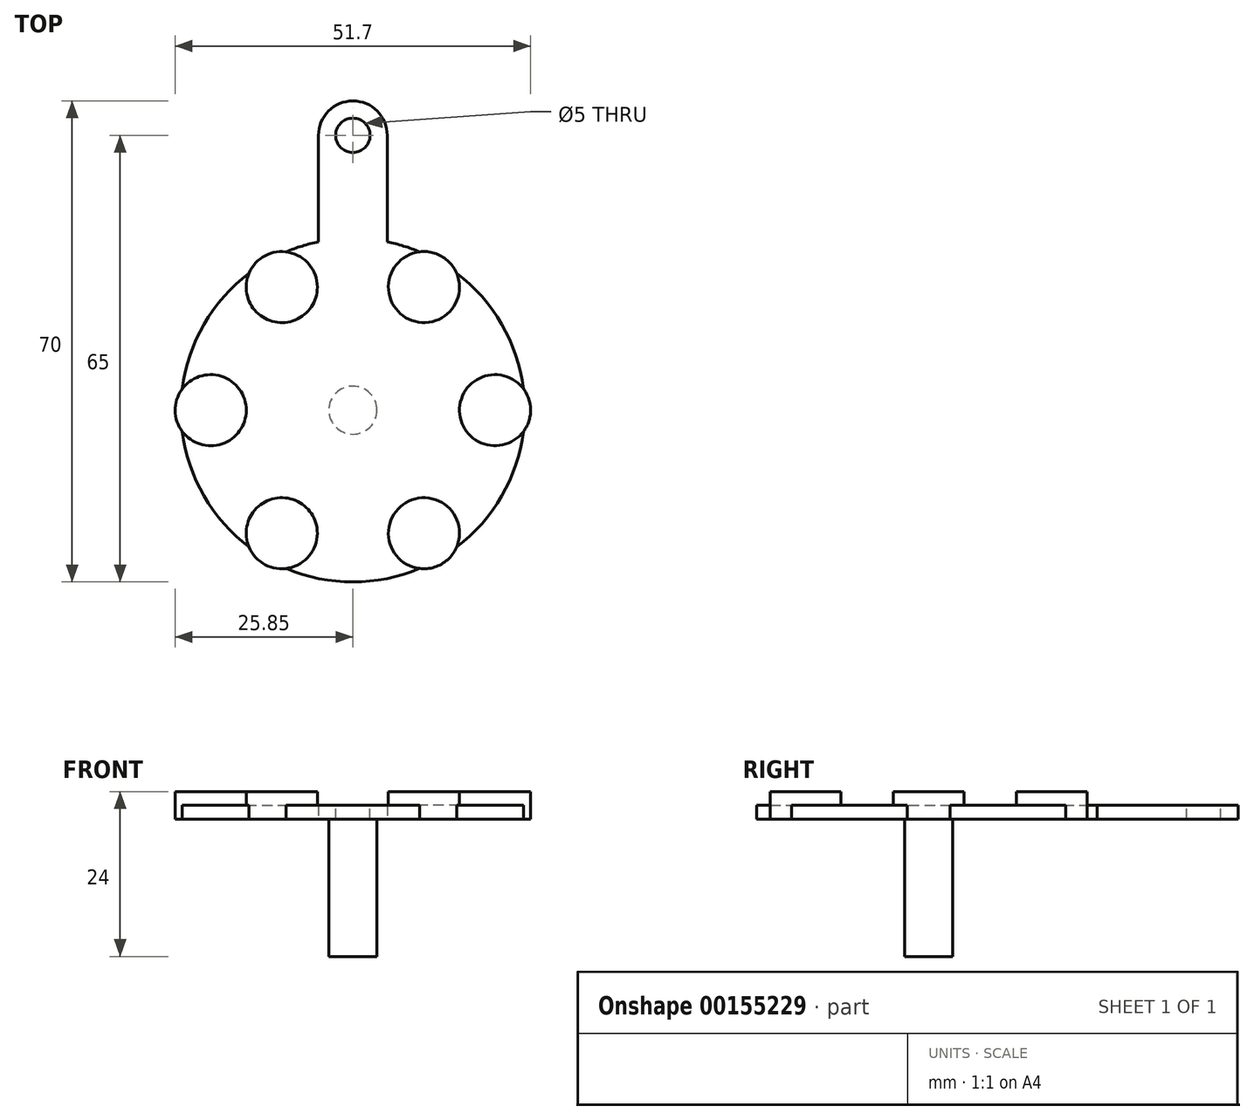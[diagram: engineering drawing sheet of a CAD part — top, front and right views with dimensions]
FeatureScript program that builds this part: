
annotation { "Feature Type Name" : "Feature", "Feature Type Description" : "" }
export const myFeature = defineFeature(function(context is Context, id is Id, definition is map)
    precondition{}
    {
        {
            var Q0;
            Q0=qCreatedBy(makeId("Top.planeOp"),FACE);
            var sketch = newSketch(context, id + "F0", { "sketchPlane" : qUnion([Q0])});
            skCircle(sketch, "E0", {"center": v(0, 0) * mm, "radius": 3.5 * mm});
            skSolve(sketch);
        }
        {
            var Q0;
            Q0 = qSketchRegion(id + "F0", true);
            extrude(context, id + "F1", {"entities" : qUnion([Q0]), "oppositeDirection" : true, "depth" : 20 * mm});
        }
        {
            var Q0;
            Q0=qCreatedBy(makeId("Top.planeOp"),FACE);
            var sketch = newSketch(context, id + "F2", { "sketchPlane" : qUnion([Q0])});
            skCircle(sketch, "E1", {"center": v(0, 0) * mm, "radius": 25 * mm});
            skSolve(sketch);
        }
        {
            var Q0;
            Q0 = qSketchRegion(id + "F2", true);
            extrude(context, id + "F3", {"entities" : qUnion([Q0]), "operationType" : NewBodyOperationType.ADD, "depth" : 2 * mm});
        }
        {
            var Q0;
            Q0=qCreatedBy(makeId("Top.planeOp"),FACE);
            var sketch = newSketch(context, id + "F4", { "sketchPlane" : qUnion([Q0])});
            skCircle(sketch, "E2", {"center": v(-20.68, 0) * mm, "radius": 5.17 * mm});
            skCircle(sketch, "E3.1.0", {"center": v(-10.34, -17.9) * mm, "radius": 5.17 * mm});
            skCircle(sketch, "E3.2.0", {"center": v(10.34, -17.9) * mm, "radius": 5.17 * mm});
            skCircle(sketch, "E3.3.0", {"center": v(20.68, 0) * mm, "radius": 5.17 * mm});
            skCircle(sketch, "E3.4.0", {"center": v(10.34, 17.9) * mm, "radius": 5.17 * mm});
            skCircle(sketch, "E3.5.0", {"center": v(-10.34, 17.9) * mm, "radius": 5.17 * mm});
            skPoint(sketch, "E3.center", {"position": v(0, 0) * mm});
            skSolve(sketch);
        }
        {
            var Q0;
            Q0 = qSketchRegion(id + "F4", true);
            extrude(context, id + "F5", {"entities" : qUnion([Q0]), "operationType" : NewBodyOperationType.ADD, "depth" : 4 * mm});
        }
        {
            var Q0;
            Q0=makeQuery(id+"F3.opExtrude","CAP_FACE",FACE,{"disambiguationData":[OSD([sQuery(id+"F2.wireOp",EDGE,"E1")])],"isStart":false});
            var sketch = newSketch(context, id + "F6", { "sketchPlane" : qUnion([Q0])});
            skLineSegment(sketch, "E4.bottom", {"start": v(-5, 0) * mm, "end": v(5, 0) * mm});
            skLineSegment(sketch, "E4.left", {"start": v(-5, 0) * mm, "end": v(-5, 40) * mm});
            skLineSegment(sketch, "E4.right", {"start": v(5, 0) * mm, "end": v(5, 40) * mm});
            skArc(sketch, "E5", {"start": v(5, 40) * mm, "mid": v(0, 45) * mm, "end": v(-5, 40) * mm});
            skCircle(sketch, "E6", {"center": v(0, 40) * mm, "radius": 2.5 * mm});
            skSolve(sketch);
        }
        {
            var Q0;
            Q0 = qSketchRegion(id + "F6", true);
            extrude(context, id + "F7", {"entities" : qUnion([Q0]), "operationType" : NewBodyOperationType.ADD, "oppositeDirection" : true, "depth" : 2 * mm});
        }
    });
